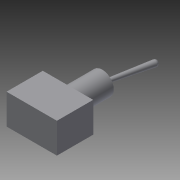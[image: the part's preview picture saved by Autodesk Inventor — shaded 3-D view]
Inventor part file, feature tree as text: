
AUTODESK INVENTOR PART (.ipt)
format: ipt  version: 2013 SP2 (Build 170200200, 200)  size: 100,352 bytes
history: native  units: mm
features: sketch x3, extrude x2, plane x1, revolve x1, projected_geometry x1
ambient origin geometry x8: Origin, YZ Plane, XZ Plane, XY Plane, X Axis, Y Axis, Z Axis, Center Point
bodies: Solid1 (feature_tree)
feature tree (8):
  extrude  "Extrusion1"  Depth=7.9mm
  extrude  "Extrusion2"  Depth=6.0mm
  plane  "Work Plane1"
  revolve  "Revolution1"  [1 undecoded]
  sketch  "Sketch1"  dims[d0=13.2mm d1=7.9mm]
  sketch  "Sketch2"  dims[d2=9.5mm d3=0.0mm d4=6.0mm]
  sketch  "Sketch3"  dims[d6=9.0mm d7=0.0mm d8=12.0mm d9=13.613568mm d10=90.0deg]
  projected_geometry  "Projected Loop1"
note: 1 required parameter value undecoded (feature->parameter linkage not recoverable at this tier; creation-order binding heuristic only, values carry confidence <= 0.55)
